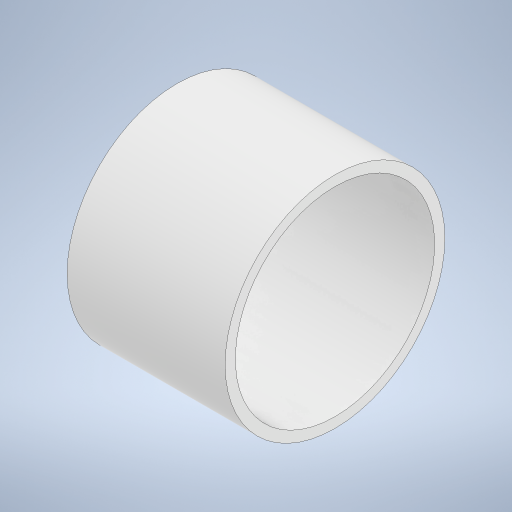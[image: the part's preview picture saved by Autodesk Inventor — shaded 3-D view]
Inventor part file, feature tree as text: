
AUTODESK INVENTOR PART (.ipt)
format: ipt  version: 2023 (Build 270158030, 158C)  size: 227,328 bytes
history: native  units: in
note: dims shown in document units (in); Inventor stores cm internally (conversion verified against a paired STEP export)
features: extrude x1, sketch x1
ambient origin geometry x8: Origin, YZ Plane, XZ Plane, XY Plane, X Axis, Y Axis, Z Axis, Center Point
bodies: Solid1 (feature_tree)
feature tree (2):
  extrude  "Extrusion1"  Depth=4.0in
  sketch  "Sketch1"  dims[d0=5.047in d1=0.258in d2=4.0in d3=0.0in]
